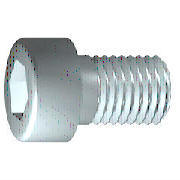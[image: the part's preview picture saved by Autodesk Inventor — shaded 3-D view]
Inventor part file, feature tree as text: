
AUTODESK INVENTOR PART (.ipt)
format: ipt  version: 2013 (Build 170138000, 138)  size: 193,024 bytes
history: native  units: mm (DEFAULTED — no unit token found)
features: sketch x2, extrude x1, plane x1, fillet x1
ambient origin geometry x7: Origin, YZ Plane, XY Plane, X Axis, Y Axis, Z Axis, Center Point
bodies: Solid1 (feature_tree), Body (feature_tree)
feature tree (5):
  extrude  "Slot"  Depth=0.429515mm
  plane  "Work Plane1"
  fillet  "Fillet2"  Radius=4.0mm
  sketch  "Sketch1"  dims[d1=10.170585mm d2=0.429515mm d3=4.0mm]
  sketch  "Sketch2"  dims[d4=2.0mm d5=60.0deg d6=4.0mm d7=4.0mm d8=3.464102mm d9=7.0mm d10=90.0deg d11=10.0mm d12=0.0mm d13=10.170585mm d14=0.0mm d15=0.429415mm d16=0.429415mm d17=0.4mm d19=0.0mm d26=12.0mm d27=45.0deg d28=0.0mm d29=0.0mm d30=0.1mm]
